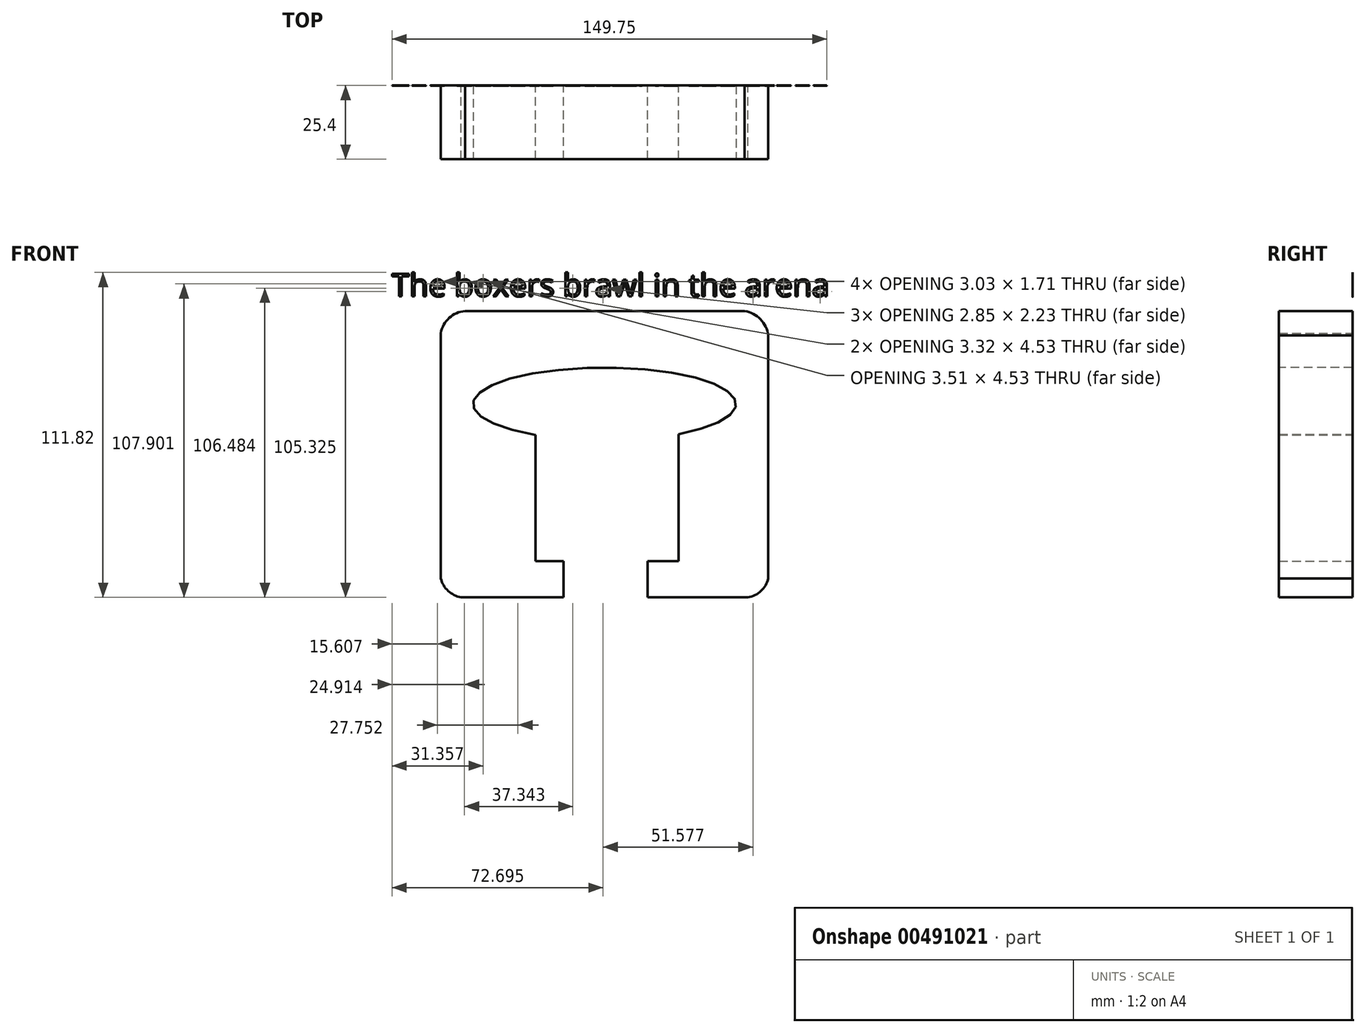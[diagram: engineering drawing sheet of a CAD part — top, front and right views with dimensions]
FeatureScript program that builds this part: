
annotation { "Feature Type Name" : "Feature", "Feature Type Description" : "" }
export const myFeature = defineFeature(function(context is Context, id is Id, definition is map)
    precondition{}
    {
        {
            var Q0;
            Q0=qCreatedBy(makeId("Front.planeOp"),FACE);
            var sketch = newSketch(context, id + "F0", { "sketchPlane" : qUnion([Q0])});
            skEllipse(sketch, "E0", {"center": v(0, 0) * mm, "majorRadius": 45.3 * mm, "minorRadius": 12.53 * mm, "majorAxis": v(1, 0)});
            skLineSegment(sketch, "E1", {"start": v(-23.79, -10.66) * mm, "end": v(-23.79, -54.06) * mm});
            skLineSegment(sketch, "E2", {"start": v(-23.79, -54.06) * mm, "end": v(25.48, -54.06) * mm});
            skLineSegment(sketch, "E3", {"start": v(25.48, -54.06) * mm, "end": v(25.48, -10.36) * mm});
            skLineSegment(sketch, "E4", {"start": v(-56.39, -66.55) * mm, "end": v(-14.15, -66.55) * mm});
            skLineSegment(sketch, "E5", {"start": v(-14.15, -66.55) * mm, "end": v(-14.15, -54.06) * mm});
            skLineSegment(sketch, "E6", {"start": v(-56.39, -66.55) * mm, "end": v(-56.39, 32) * mm});
            skLineSegment(sketch, "E7", {"start": v(-56.39, 32) * mm, "end": v(61.98, 32) * mm});
            skLineSegment(sketch, "E8", {"start": v(-45.3, 0) * mm, "end": v(-56.39, 0) * mm});
            skLineSegment(sketch, "E9", {"start": v(45.3, 0) * mm, "end": v(56.39, 0) * mm});
            skPoint(sketch, "E9.endSnap0", {"position": v(45.3, 0) * mm});
            skLineSegment(sketch, "E10", {"start": v(56.39, 0) * mm, "end": v(56.39, 32) * mm});
            skLineSegment(sketch, "E11", {"start": v(14.79, -66.55) * mm, "end": v(14.79, -54.06) * mm});
            skLineSegment(sketch, "E12", {"start": v(56.39, 0) * mm, "end": v(56.39, -66.55) * mm});
            skLineSegment(sketch, "E13", {"start": v(14.79, -66.55) * mm, "end": v(56.39, -66.55) * mm});
            skArc(sketch, "E14", {"start": v(-46.74, 32) * mm, "mid": v(-54.16, 29) * mm, "end": v(-56.39, 21.31) * mm});
            skArc(sketch, "E15", {"start": v(56.39, 21.31) * mm, "mid": v(53.5, 29.41) * mm, "end": v(45.3, 32) * mm});
            skArc(sketch, "E16", {"start": v(-56.39, -60.1) * mm, "mid": v(-52.68, -65.27) * mm, "end": v(-46.45, -66.55) * mm});
            skLineSegment(sketch, "E17", {"start": v(-56.39, -60.1) * mm, "end": v(56.39, -60.1) * mm});
            skArc(sketch, "E18", {"start": v(46.68, -66.55) * mm, "mid": v(52.8, -65.23) * mm, "end": v(56.39, -60.1) * mm});
            skSolve(sketch);
        }
        {
            var Q0;
            {var subQ1=sQuery(id+"F0.wireOp",EDGE,"E1");Q0=makeQuery(id+"F0.imprint","IMPRINT",FACE,{"disambiguationData":[TD([[makeQuery(id+"F0.imprint","IMPRINT",EDGE,{"derivedFrom":subQ1}),-1.0]])]});}
            var Q1;
            {var subQ1=sQuery(id+"F0.wireOp",EDGE,"E8");Q1=makeQuery(id+"F0.imprint","IMPRINT",FACE,{"disambiguationData":[TD([[makeQuery(id+"F0.imprint","IMPRINT",EDGE,{"derivedFrom":subQ1}),-1.0]])]});}
            var Q2;
            {var subQ1=sQuery(id+"F0.wireOp",EDGE,"E3");Q2=makeQuery(id+"F0.imprint","IMPRINT",FACE,{"disambiguationData":[TD([[makeQuery(id+"F0.imprint","IMPRINT",EDGE,{"derivedFrom":subQ1}),-1.0]])]});}
            var Q3;
            {var subQ1=sQuery(id+"F0.wireOp",EDGE,"E16");var subQ3=sQuery(id+"F0.wireOp",EDGE,"E4");var subQ8=makeQuery(id+"F0.imprint","INTERSECT",VERTEX,{"disambiguationData":[OD(0.0)],"derivedFrom":[subQ3,subQ1]});Q3=makeQuery(id+"F0.imprint","IMPRINT",FACE,{"disambiguationData":[TD([[makeQuery(id+"F0.imprint","IMPRINT",EDGE,{"disambiguationData":[TD([[subQ8,1.0]])],"derivedFrom":subQ3}),1.0]])]});}
            var Q4;
            {var subQ3=sQuery(id+"F0.wireOp",EDGE,"E11");var subQ5=sQuery(id+"F0.wireOp",EDGE,"E13");var subQ6=makeQuery(id+"F0.imprint","INTERSECT",VERTEX,{"derivedFrom":[subQ3,subQ5]});Q4=makeQuery(id+"F0.imprint","IMPRINT",FACE,{"disambiguationData":[TD([[makeQuery(id+"F0.imprint","IMPRINT",EDGE,{"disambiguationData":[TD([[subQ6,-1.0]])],"derivedFrom":subQ3}),-1.0]])]});}
            extrude(context, id + "F1", {"entities" : qUnion([Q0, Q1, Q2, Q3, Q4]), "depth" : 25.4 * mm});
        }
        {
            var Q0;
            Q0=qCreatedBy(makeId("Front.planeOp"),FACE);
            var sketch = newSketch(context, id + "F2", { "sketchPlane" : qUnion([Q0])});
            skText(sketch, "E19", { "text": "The boxers brawl in the arena ", "fontName": "OpenSans-Regular.ttf"});
            const initialGuessF2  = {"E19": [-0.07326, 0.03704, 1, 0, 0.0078]};
            skSetInitialGuess(sketch, initialGuessF2);
            skSolve(sketch);
        }
        {
            var Q0;
            Q0 = qSketchRegion(id + "F2", true);
            extrude(context, id + "F3", {"entities" : qUnion([Q0]), "depth" : 0.05 * mm});
        }
    });
